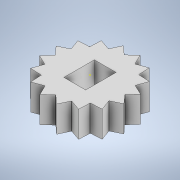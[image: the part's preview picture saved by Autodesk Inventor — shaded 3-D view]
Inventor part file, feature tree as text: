
AUTODESK INVENTOR PART (.ipt)
format: ipt  version: 2020 (Build 240168000, 168)  size: 224,256 bytes
history: native  units: mm
features: sketch x5, extrude x4, pattern_circular x2
ambient origin geometry x8: Origin, YZ Plane, XZ Plane, XY Plane, X Axis, Y Axis, Z Axis, Center Point
bodies: Solid1 (feature_tree)
feature tree (11):
  extrude  "Extrusion1"  Depth=7.0mm
  extrude  "Extrusion2"  Depth=5.0mm
  pattern_circular  "Circular Pattern1"  [2 undecoded]
  extrude  "Extrusion3"  Depth=6.0mm TaperAngle=360.0deg
  extrude  "Extrusion4"  Depth=6.0mm TaperAngle=0.0deg
  pattern_circular  "Circular Pattern2"  [2 undecoded]
  sketch  "Sketch5"  dims[d12=1.0mm d13=8.726646mm d14=22.68928mm d15=0.5mm d16=2.0mm d17=0.0mm d18=210.0mm d19=360.0deg d21=6.0mm d22=0.0mm d23=6.0mm d24=0.0mm d25=160.0mm d26=360.0deg]
  sketch  "Sketch1"  dims[d0=1.0mm d1=8.726646mm d2=22.68928mm d3=0.5mm d6=7.0mm]
  sketch  "Sketch2"  dims[d7=5.0mm d8=3.5mm]
  sketch  "Sketch3"  dims[d9=2.5mm]
  sketch  "Sketch4"  dims[d10=6.0mm d11=0.0mm]
note: 4 required parameter values undecoded (feature->parameter linkage not recoverable at this tier; creation-order binding heuristic only, values carry confidence <= 0.55)
